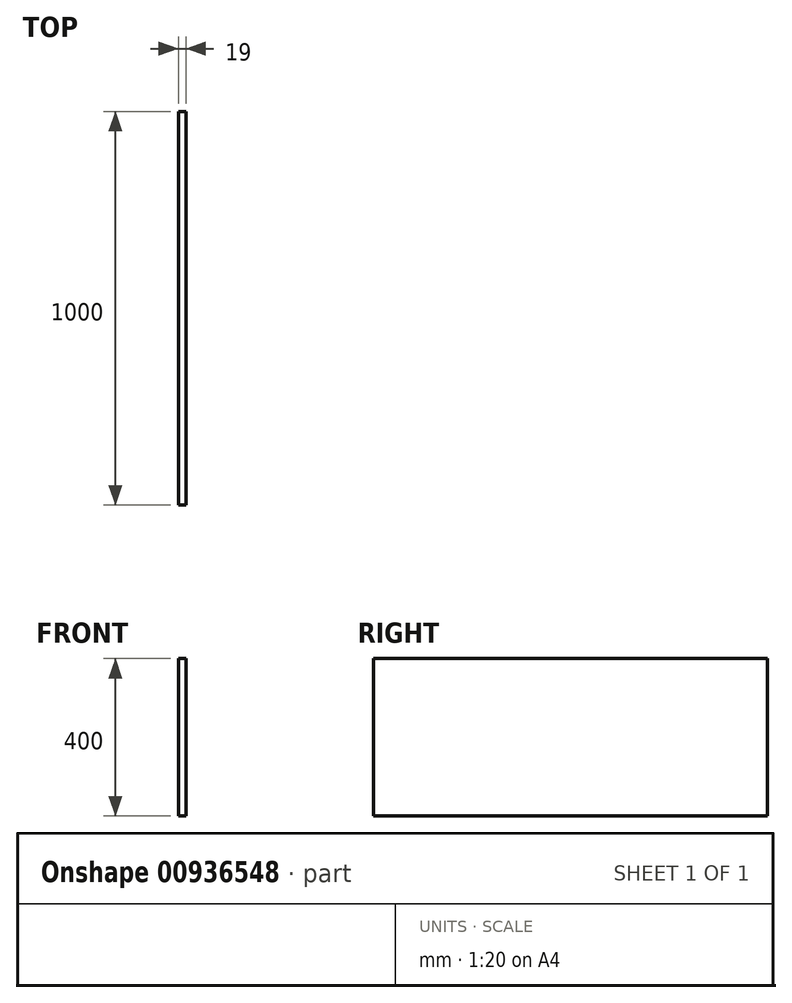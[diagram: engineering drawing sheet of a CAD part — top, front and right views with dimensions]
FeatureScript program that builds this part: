
annotation { "Feature Type Name" : "Feature", "Feature Type Description" : "" }
export const myFeature = defineFeature(function(context is Context, id is Id, definition is map)
    precondition{}
    {
        {
            var Q0;
            Q0=qCreatedBy(makeId("Front.planeOp"),FACE);
            var sketch = newSketch(context, id + "F0", { "sketchPlane" : qUnion([Q0])});
            skLineSegment(sketch, "E0.bottom", {"start": v(9.5, 200) * mm, "end": v(-9.5, 200) * mm});
            skLineSegment(sketch, "E0.top", {"start": v(9.5, -200) * mm, "end": v(-9.5, -200) * mm});
            skLineSegment(sketch, "E0.left", {"start": v(9.5, 200) * mm, "end": v(9.5, -200) * mm});
            skLineSegment(sketch, "E0.right", {"start": v(-9.5, 200) * mm, "end": v(-9.5, -200) * mm});
            skPoint(sketch, "E0.middle", {"position": v(0, 0) * mm});
            skSolve(sketch);
        }
        {
            var Q0;
            Q0=qSketchRegion(id+"F0",true);
            extrude(context, id + "F1", {"entities" : qUnion([Q0]), "depth" : 1000 * mm, "offsetDistance" : 25 * mm});
        }
    });
